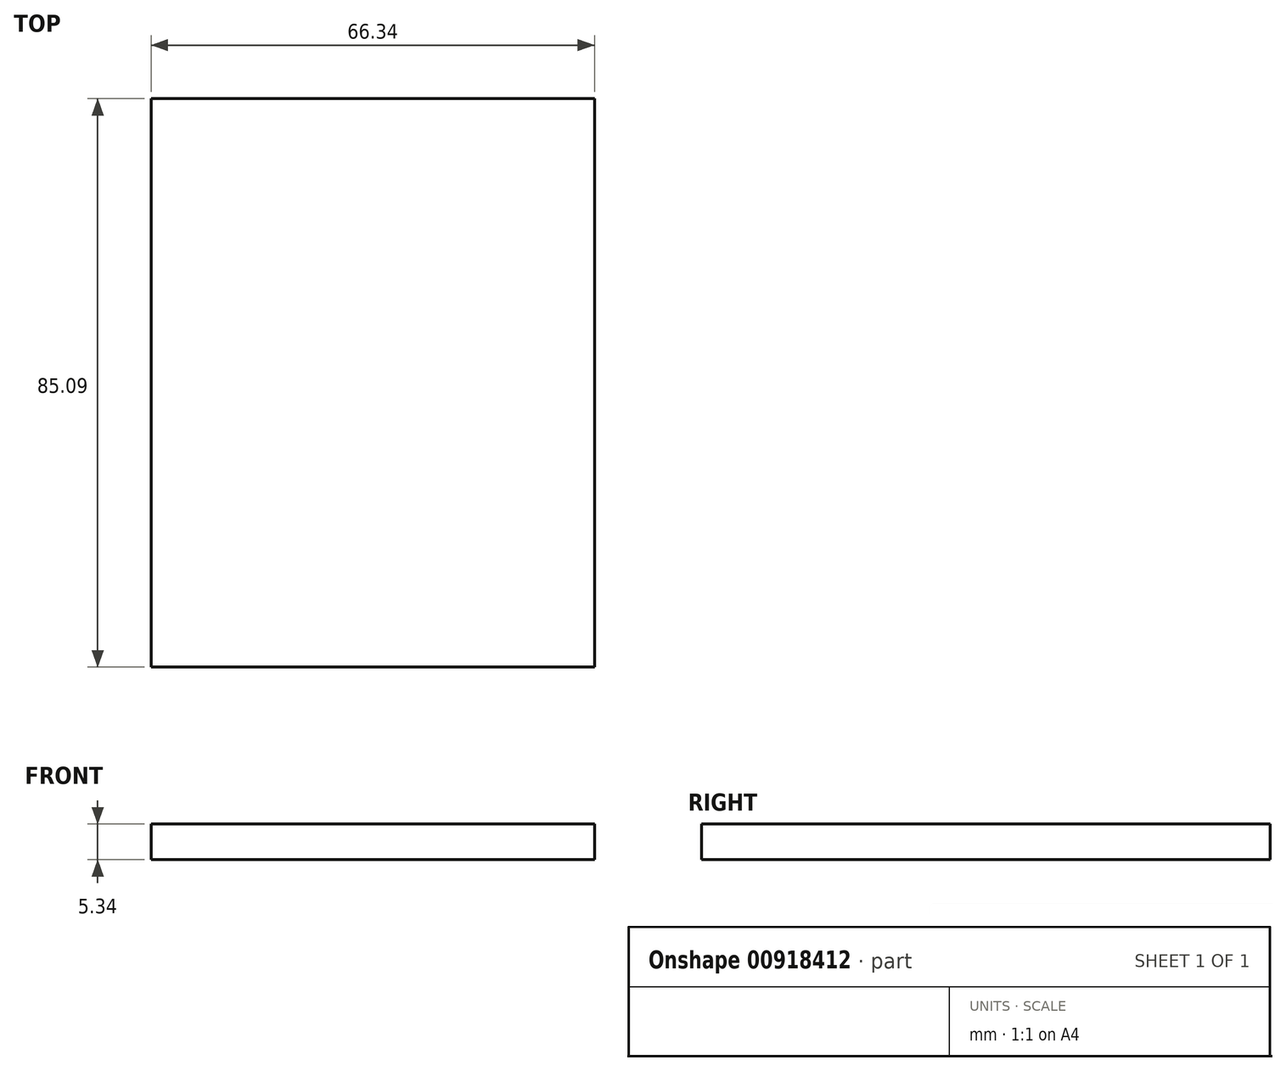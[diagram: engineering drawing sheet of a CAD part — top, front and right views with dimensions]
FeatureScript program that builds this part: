
annotation { "Feature Type Name" : "Feature", "Feature Type Description" : "" }
export const myFeature = defineFeature(function(context is Context, id is Id, definition is map)
    precondition{}
    {
        {
            var Q0;
            Q0=qCreatedBy(makeId("Front.planeOp"),FACE);
            var sketch = newSketch(context, id + "F0", { "sketchPlane" : qUnion([Q0])});
            skLineSegment(sketch, "E0.bottom", {"start": v(33, 116.74) * mm, "end": v(-33.34, 116.74) * mm});
            skLineSegment(sketch, "E0.top", {"start": v(33, 122.08) * mm, "end": v(-33.34, 122.08) * mm});
            skLineSegment(sketch, "E0.left", {"start": v(33, 116.74) * mm, "end": v(33, 122.08) * mm});
            skLineSegment(sketch, "E0.right", {"start": v(-33.34, 116.74) * mm, "end": v(-33.34, 122.08) * mm});
            skSolve(sketch);
        }
        {
            var Q0;
            Q0=makeQuery(id+"F0.imprint","IMPRINT",FACE,{"disambiguationData":[TD([[makeQuery(id+"F0.imprint","IMPRINT",EDGE,{"derivedFrom":sQuery(id+"F0.wireOp",EDGE,"E0.bottom")}),-1.0]])]});
            extrude(context, id + "F1", {"entities" : qUnion([Q0]), "depth" : 85.1 * mm, "offsetDistance" : 25.4 * mm});
        }
    });
